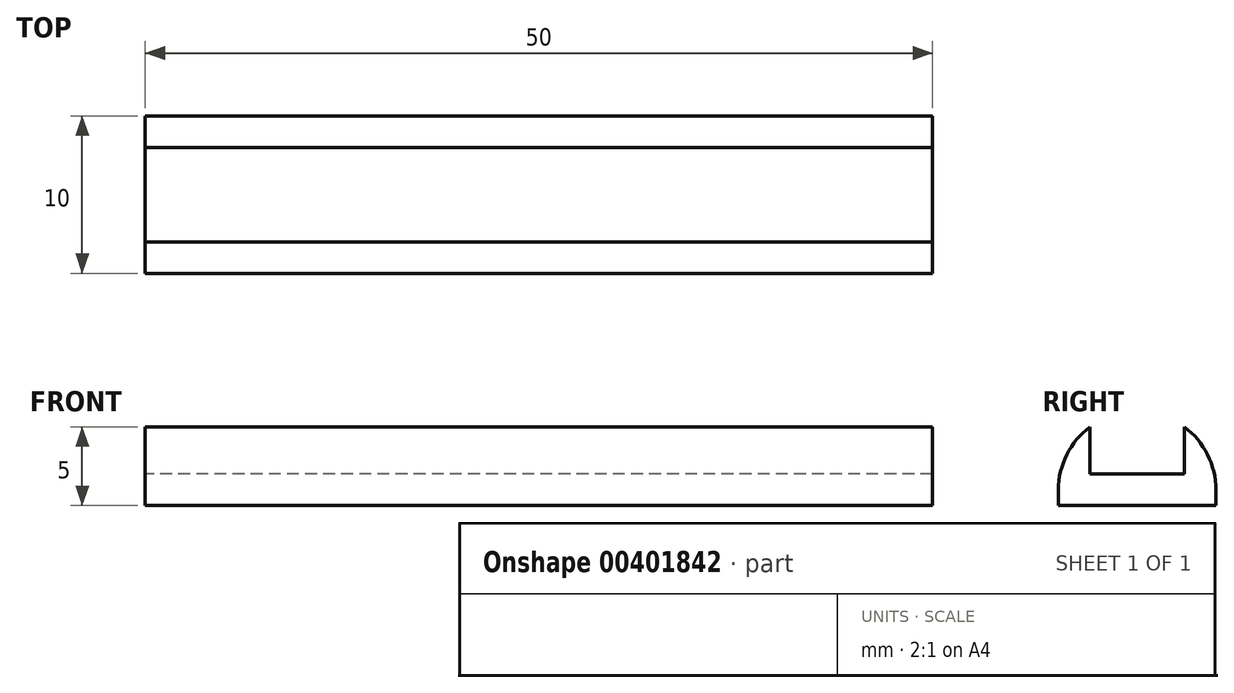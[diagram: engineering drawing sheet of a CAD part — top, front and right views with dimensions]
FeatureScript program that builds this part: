
annotation { "Feature Type Name" : "Feature", "Feature Type Description" : "" }
export const myFeature = defineFeature(function(context is Context, id is Id, definition is map)
    precondition{}
    {
        {
            var Q0;
            Q0=qCreatedBy(makeId("Top.planeOp"),FACE);
            var sketch = newSketch(context, id + "F0", { "sketchPlane" : qUnion([Q0])});
            skLineSegment(sketch, "E0.bottom", {"start": v(-25, 5) * mm, "end": v(25, 5) * mm});
            skLineSegment(sketch, "E0.top", {"start": v(-25, -5) * mm, "end": v(25, -5) * mm});
            skLineSegment(sketch, "E0.left", {"start": v(-25, 5) * mm, "end": v(-25, -5) * mm});
            skLineSegment(sketch, "E0.right", {"start": v(25, 5) * mm, "end": v(25, -5) * mm});
            skLineSegment(sketch, "E1", {"start": v(-25, 3) * mm, "end": v(25, 3) * mm});
            skLineSegment(sketch, "E2", {"start": v(-25, -3) * mm, "end": v(25, -3) * mm});
            skSolve(sketch);
        }
        {
            var Q0;
            Q0 = qSketchRegion(id + "F3Lll8WSsEeu1wO_0", true);
            var Q1;
            {var subQ0=sQuery(id+"F0.wireOp",EDGE,"E1");Q1=makeQuery(id+"F0.imprint","IMPRINT",FACE,{"disambiguationData":[TD([[makeQuery(id+"F0.imprint","IMPRINT",EDGE,{"derivedFrom":subQ0}),-1.0]])]});}
            var Q2;
            {var subQ0=sQuery(id+"F0.wireOp",EDGE,"E0.bottom");Q2=makeQuery(id+"F0.imprint","IMPRINT",FACE,{"disambiguationData":[TD([[makeQuery(id+"F0.imprint","IMPRINT",EDGE,{"derivedFrom":subQ0}),-1.0]])]});}
            var Q3;
            {var subQ0=sQuery(id+"F0.wireOp",EDGE,"E0.top");Q3=makeQuery(id+"F0.imprint","IMPRINT",FACE,{"disambiguationData":[TD([[makeQuery(id+"F0.imprint","IMPRINT",EDGE,{"derivedFrom":subQ0}),1.0]])]});}
            extrude(context, id + "F1", {"entities" : qUnion([Q0, Q1, Q2, Q3]), "depth" : 2 * mm});
        }
        {
            var Q0;
            {var subQ0=sQuery(id+"F0.wireOp",EDGE,"E0.bottom");Q0=makeQuery(id+"F0.imprint","IMPRINT",FACE,{"disambiguationData":[TD([[makeQuery(id+"F0.imprint","IMPRINT",EDGE,{"derivedFrom":subQ0}),-1.0]])]});}
            var Q1;
            {var subQ0=sQuery(id+"F0.wireOp",EDGE,"E0.top");Q1=makeQuery(id+"F0.imprint","IMPRINT",FACE,{"disambiguationData":[TD([[makeQuery(id+"F0.imprint","IMPRINT",EDGE,{"derivedFrom":subQ0}),1.0]])]});}
            extrude(context, id + "F2", {"entities" : qUnion([Q0, Q1]), "operationType" : NewBodyOperationType.ADD, "depth" : 5 * mm});
        }
        {
            var Q0;
            Q0=makeQuery(id+"F2.opExtrude","CAP_EDGE",EDGE,{"disambiguationData":[OSD([sQuery(id+"F0.wireOp",EDGE,"E0.top")])],"isStart":false});
            var Q1;
            Q1=makeQuery(id+"F2.opExtrude","CAP_EDGE",EDGE,{"disambiguationData":[OSD([sQuery(id+"F0.wireOp",EDGE,"E0.bottom")])],"isStart":false});
            fillet(context, id + "F3", {"entities" : qUnion([Q0, Q1]), "radius" : 5 * mm, "tangentPropagation" : true, "allowEdgeOverflow" : false});
        }
    });
